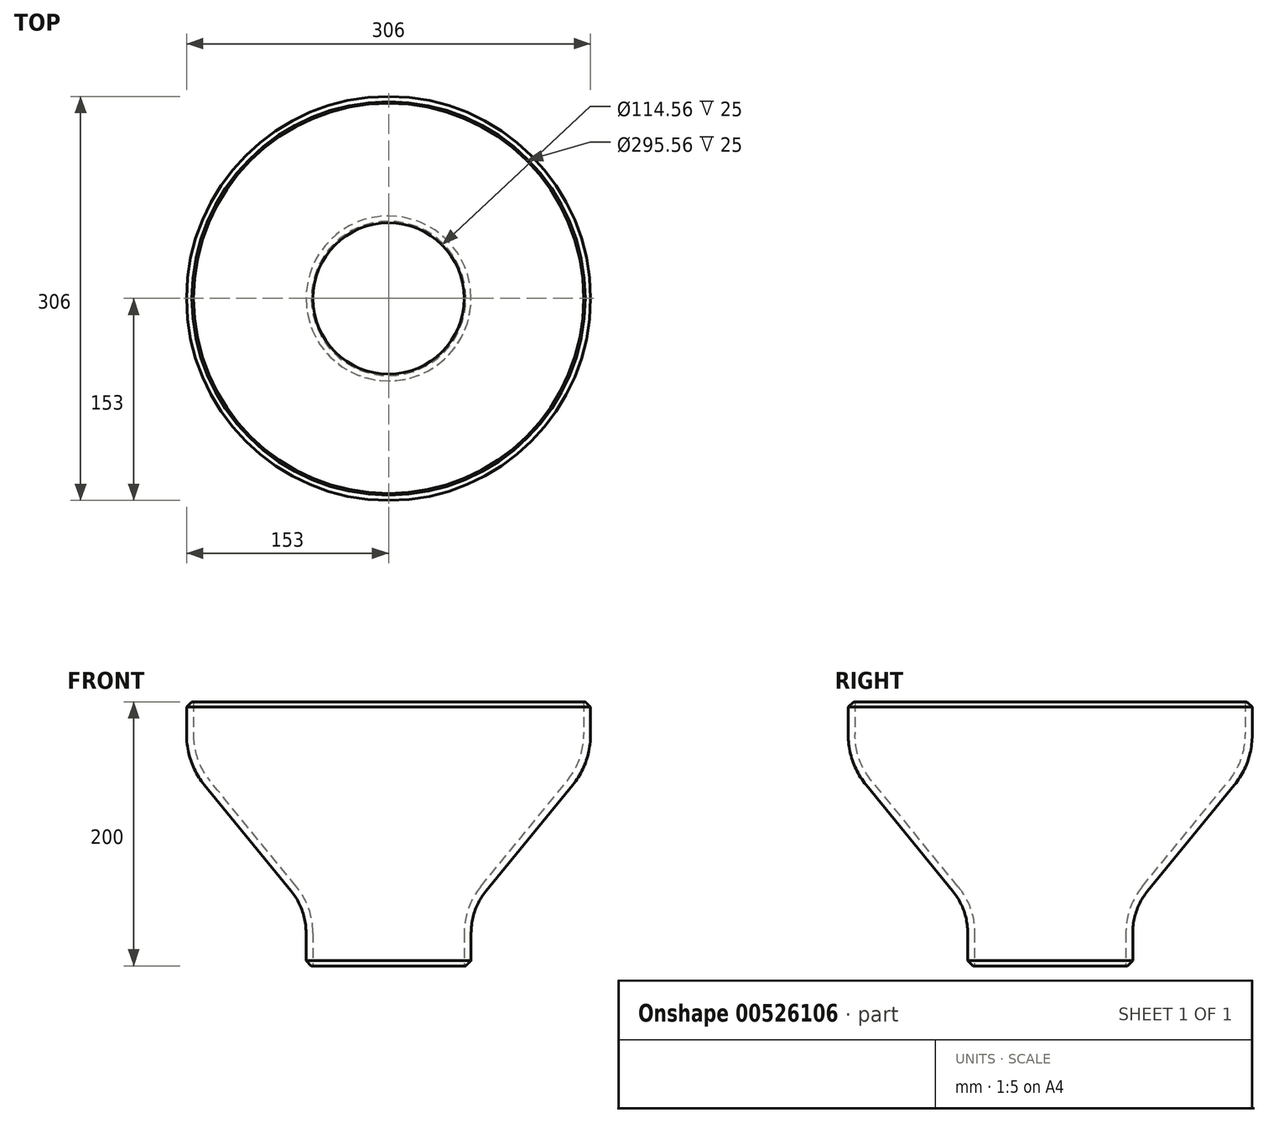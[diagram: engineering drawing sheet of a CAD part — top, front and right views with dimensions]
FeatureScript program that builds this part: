
annotation { "Feature Type Name" : "Feature", "Feature Type Description" : "" }
export const myFeature = defineFeature(function(context is Context, id is Id, definition is map)
    precondition{}
    {
        {
            var Q0;
            Q0=qCreatedBy(makeId("Front.planeOp"),FACE);
            var sketch = newSketch(context, id + "F0", { "sketchPlane" : qUnion([Q0])});
            skLineSegment(sketch, "E0", {"start": v(0, -59.44) * mm, "end": v(0, 124.97) * mm, "construction": true});
            skLineSegment(sketch, "E1", {"start": v(-153, 125.35) * mm, "end": v(-153, 100.35) * mm});
            skLineSegment(sketch, "E2", {"start": v(-62.5, -74.65) * mm, "end": v(-62.5, -49.65) * mm});
            skLineSegment(sketch, "E3", {"start": v(-73.78, -18.01) * mm, "end": v(-139.47, 62.4) * mm});
            skPoint(sketch, "E4.visualSharp", {"position": v(-153, 78.96) * mm});
            skArc(sketch, "E4.filletArc", {"start": v(-153, 100.35) * mm, "mid": v(-149.52, 80.2) * mm, "end": v(-139.47, 62.4) * mm});
            skPoint(sketch, "E5.visualSharp", {"position": v(-62.5, -31.82) * mm});
            skArc(sketch, "E5.filletArc", {"start": v(-62.5, -49.65) * mm, "mid": v(-65.4, -32.85) * mm, "end": v(-73.78, -18.01) * mm});
            skLineSegment(sketch, "E6.0", {"start": v(-57.28, -74.65) * mm, "end": v(-57.28, -49.65) * mm});
            skLineSegment(sketch, "E6.1", {"start": v(-147.78, 125.35) * mm, "end": v(-147.78, 100.35) * mm});
            skArc(sketch, "E6.2", {"start": v(-147.78, 100.35) * mm, "mid": v(-144.6, 81.96) * mm, "end": v(-135.42, 65.7) * mm});
            skLineSegment(sketch, "E6.3", {"start": v(-69.74, -14.71) * mm, "end": v(-135.42, 65.7) * mm});
            skArc(sketch, "E6.4", {"start": v(-57.28, -49.65) * mm, "mid": v(-60.49, -31.1) * mm, "end": v(-69.74, -14.71) * mm});
            skLineSegment(sketch, "E7", {"start": v(-153, 125.35) * mm, "end": v(-147.78, 125.35) * mm});
            skLineSegment(sketch, "E8", {"start": v(-62.5, -74.65) * mm, "end": v(-57.28, -74.65) * mm});
            skSolve(sketch);
        }
        {
            var Q0;
            Q0=makeQuery(id+"F0.imprint","IMPRINT",FACE,{"disambiguationData":[TD([[makeQuery(id+"F0.imprint","IMPRINT",EDGE,{"derivedFrom":sQuery(id+"F0.wireOp",EDGE,"E1")}),1.0]])]});
            var Q1;
            Q1=sQuery(id+"F0.wireOp",EDGE,"E0");
            revolve(context, id + "F1", {"entities" : qUnion([Q0]), "axis" : qUnion([Q1]), "revolveType" : RevolveType.FULL});
        }
        {
            var Q0;
            Q0=makeQuery(id+"F1.opRevolve","SWEPT_EDGE",EDGE,{"disambiguationData":[OSD([sQuery(id+"F0.wireOp",EDGE,"E1"),sQuery(id+"F0.wireOp",EDGE,"E7")])]});
            var Q1;
            Q1=makeQuery(id+"F1.opRevolve","SWEPT_EDGE",EDGE,{"disambiguationData":[OSD([sQuery(id+"F0.wireOp",EDGE,"E2"),sQuery(id+"F0.wireOp",EDGE,"E8")])]});
            chamfer(context, id + "F2", {"entities" : qUnion([Q0, Q1]), "width" : 4 * mm, "tangentPropagation" : true});
        }
    });
